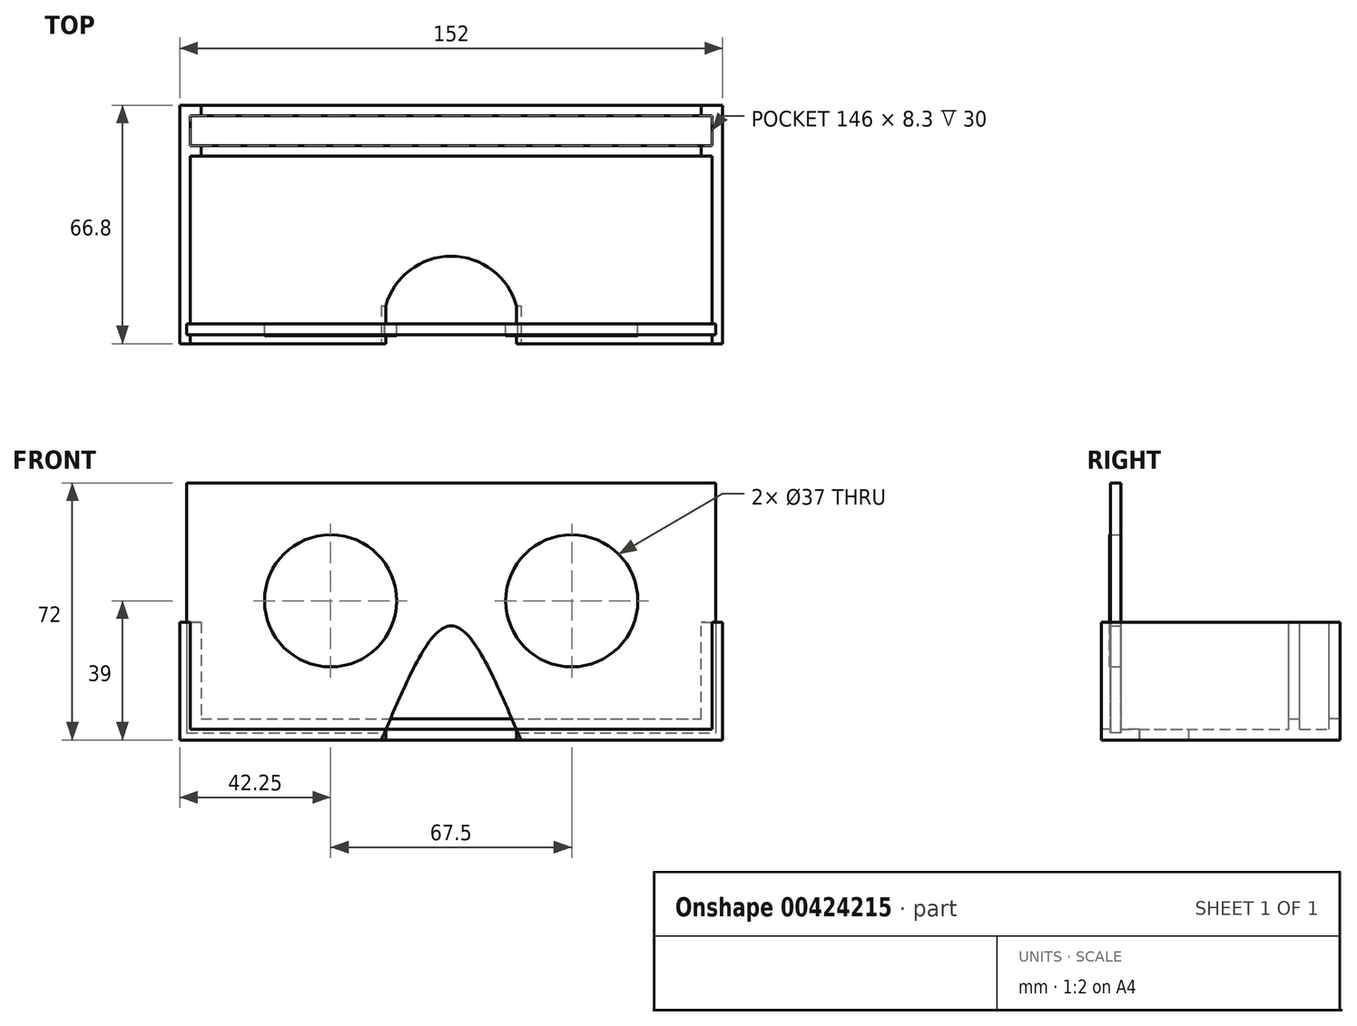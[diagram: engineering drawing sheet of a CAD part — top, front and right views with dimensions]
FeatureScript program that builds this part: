
annotation { "Feature Type Name" : "Feature", "Feature Type Description" : "" }
export const myFeature = defineFeature(function(context is Context, id is Id, definition is map)
    precondition{}
    {
        {
            var Q0;
            Q0=qCreatedBy(makeId("Front.planeOp"),FACE);
            var sketch = newSketch(context, id + "F0", { "sketchPlane" : qUnion([Q0])});
            skCircle(sketch, "E0", {"center": v(-33.75, 0) * mm, "radius": 18.5 * mm});
            skCircle(sketch, "E1", {"center": v(33.75, 0) * mm, "radius": 18.5 * mm});
            skLineSegment(sketch, "E2", {"start": v(0, 0) * mm, "end": v(15.25, 0) * mm});
            skLineSegment(sketch, "E3", {"start": v(0, 0) * mm, "end": v(-15.25, 0) * mm});
            skSolve(sketch);
        }
        {
            var Q0;
            Q0=makeQuery(id+"F0.imprint","IMPRINT",FACE,{"disambiguationData":[TD([[makeQuery(id+"F0.imprint","IMPRINT",EDGE,{"derivedFrom":sQuery(id+"F0.wireOp",EDGE,"E1")}),1.0]])]});
            var Q1;
            Q1=makeQuery(id+"F0.imprint","IMPRINT",FACE,{"disambiguationData":[TD([[makeQuery(id+"F0.imprint","IMPRINT",EDGE,{"derivedFrom":sQuery(id+"F0.wireOp",EDGE,"E0")}),1.0]])]});
            extrude(context, id + "F1", {"entities" : qUnion([Q0, Q1]), "depth" : 3.2 * mm});
        }
        {
            var Q0;
            Q0=qCreatedBy(makeId("Front.planeOp"),FACE);
            cPlane(context, id + "F2", {"entities" : qUnion([Q0]), "cplaneType" : CPlaneType.OFFSET, "offset" : 50 * mm, "oppositeDirection" : true, "width" : 150 * mm, "height" : 150 * mm});
        }
        {
            var Q0;
            Q0=qCreatedBy(id+"F2.planeOp",FACE);
            var sketch = newSketch(context, id + "F3", { "sketchPlane" : qUnion([Q0])});
            skLineSegment(sketch, "E4.bottom", {"start": v(-71.2, 34.8) * mm, "end": v(71.2, 34.8) * mm});
            skLineSegment(sketch, "E4.top", {"start": v(-71.2, -34.8) * mm, "end": v(71.2, -34.8) * mm});
            skLineSegment(sketch, "E4.left", {"start": v(-71.2, 34.8) * mm, "end": v(-71.2, -34.8) * mm});
            skLineSegment(sketch, "E4.right", {"start": v(71.2, 34.8) * mm, "end": v(71.2, -34.8) * mm});
            skLineSegment(sketch, "E5", {"start": v(0, 0) * mm, "end": v(0, 34.8) * mm, "construction": true});
            skLineSegment(sketch, "E6", {"start": v(0, 0) * mm, "end": v(-71.2, 0) * mm, "construction": true});
            skSolve(sketch);
        }
        {
            var Q0;
            Q0=qCreatedBy(id+"F2.planeOp",FACE);
            var sketch = newSketch(context, id + "F4", { "sketchPlane" : qUnion([Q0])});
            skLineSegment(sketch, "E7", {"start": v(-73, -6) * mm, "end": v(-76, -6) * mm});
            skLineSegment(sketch, "E8", {"start": v(-76, -6) * mm, "end": v(-76, -39) * mm});
            skLineSegment(sketch, "E9", {"start": v(-76, -39) * mm, "end": v(76, -39) * mm});
            skLineSegment(sketch, "E10", {"start": v(76, -39) * mm, "end": v(76, -6) * mm});
            skLineSegment(sketch, "E11", {"start": v(76, -6) * mm, "end": v(73, -6) * mm});
            skLineSegment(sketch, "E12", {"start": v(73, -6) * mm, "end": v(73, -36) * mm});
            skLineSegment(sketch, "E13", {"start": v(73, -36) * mm, "end": v(-73, -36) * mm});
            skLineSegment(sketch, "E14", {"start": v(-73, -36) * mm, "end": v(-73, -6) * mm});
            skLineSegment(sketch, "E15", {"start": v(-73, -6) * mm, "end": v(73, -6) * mm});
            skLineSegment(sketch, "E16", {"start": v(0, -36) * mm, "end": v(0, 0) * mm});
            skSolve(sketch);
        }
        {
            var Q0;
            Q0=makeQuery(id+"F4.imprint","IMPRINT",FACE,{"disambiguationData":[TD([[makeQuery(id+"F4.imprint","IMPRINT",EDGE,{"derivedFrom":sQuery(id+"F4.wireOp",EDGE,"E7")}),1.0]])]});
            extrude(context, id + "F5", {"entities" : qUnion([Q0]), "depth" : 55.5 * mm, "hasSecondDirection" : true, "secondDirectionOppositeDirection" : true, "secondDirectionDepth" : 11.3 * mm});
        }
        {
            var Q0;
            Q0=qCreatedBy(makeId("Front.planeOp"),FACE);
            var sketch = newSketch(context, id + "F6", { "sketchPlane" : qUnion([Q0])});
            skCircle(sketch, "E17", {"center": v(-33.75, 0) * mm, "radius": 18.5 * mm});
            skCircle(sketch, "E18", {"center": v(33.75, 0) * mm, "radius": 18.5 * mm});
            skLineSegment(sketch, "E19", {"start": v(-15.25, 0) * mm, "end": v(0, 0) * mm});
            skLineSegment(sketch, "E20", {"start": v(15.25, 0) * mm, "end": v(0, 0) * mm});
            skLineSegment(sketch, "E21.bottom", {"start": v(-74, 33) * mm, "end": v(74, 33) * mm});
            skLineSegment(sketch, "E21.top", {"start": v(-74, -37) * mm, "end": v(74, -37) * mm});
            skLineSegment(sketch, "E21.left", {"start": v(-74, 33) * mm, "end": v(-74, -37) * mm});
            skLineSegment(sketch, "E21.right", {"start": v(74, 33) * mm, "end": v(74, -37) * mm});
            skLineSegment(sketch, "E22", {"start": v(0, 0) * mm, "end": v(0, 33) * mm});
            skLineSegment(sketch, "E23.top", {"start": v(-74, 43) * mm, "end": v(74, 43) * mm});
            skLineSegment(sketch, "E23.left", {"start": v(-74, 33) * mm, "end": v(-74, 43) * mm});
            skLineSegment(sketch, "E23.right", {"start": v(74, 33) * mm, "end": v(74, 43) * mm});
            skSolve(sketch);
        }
        {
            var Q0;
            Q0=makeQuery(id+"F6.imprint","IMPRINT",FACE,{"disambiguationData":[TD([[makeQuery(id+"F6.imprint","IMPRINT",EDGE,{"derivedFrom":sQuery(id+"F6.wireOp",EDGE,"E17")}),-1.0]])]});
            var Q1;
            Q1=makeQuery(id+"F6.imprint","IMPRINT",FACE,{"disambiguationData":[TD([[makeQuery(id+"F6.imprint","IMPRINT",EDGE,{"derivedFrom":sQuery(id+"F6.wireOp",EDGE,"E23.top")}),-1.0]])]});
            extrude(context, id + "F7", {"entities" : qUnion([Q0, Q1]), "operationType" : NewBodyOperationType.REMOVE, "depth" : 3 * mm});
        }
        {
            var Q0;
            Q0=makeQuery(id+"F6.imprint","IMPRINT",FACE,{"disambiguationData":[TD([[makeQuery(id+"F6.imprint","IMPRINT",EDGE,{"derivedFrom":sQuery(id+"F6.wireOp",EDGE,"E17")}),-1.0]])]});
            extrude(context, id + "F8", {"entities" : qUnion([Q0]), "depth" : 3 * mm});
        }
        {
            var Q0;
            Q0=qCreatedBy(makeId("Front.planeOp"),FACE);
            var sketch = newSketch(context, id + "F9", { "sketchPlane" : qUnion([Q0])});
            skFitSpline(sketch, "E24", {"points": [v(-20, -40) * mm, v(0, -7) * mm, v(20, -40) * mm], "startDerivative": vector(42.04, 95.95) * mm, "endDerivative": vector(42.04, -95.95) * mm});
            skLineSegment(sketch, "E25", {"start": v(-20, -40) * mm, "end": v(20, -40) * mm});
            skLineSegment(sketch, "E26", {"start": v(-20, -40) * mm, "end": v(-13, -24) * mm});
            skLineSegment(sketch, "E27", {"start": v(13, -24) * mm, "end": v(20, -40) * mm});
            skLineSegment(sketch, "E28", {"start": v(0, -40) * mm, "end": v(0, 0) * mm});
            skSolve(sketch);
        }
        {
            var Q0;
            Q0 = qSketchRegion(id + "F9", true);
            extrude(context, id + "F10", {"entities" : qUnion([Q0]), "operationType" : NewBodyOperationType.REMOVE, "depth" : 26.3 * mm, "hasSecondDirection" : true, "secondDirectionOppositeDirection" : true, "secondDirectionDepth" : 5.1 * mm});
        }
        {
            var Q0;
            Q0=qCreatedBy(makeId("Top.planeOp"),FACE);
            var sketch = newSketch(context, id + "F11", { "sketchPlane" : qUnion([Q0])});
            skCircle(sketch, "E29", {"center": v(0, 0) * mm, "radius": 19 * mm});
            skLineSegment(sketch, "E30", {"start": v(-18.33, 5) * mm, "end": v(18.33, 5) * mm});
            skSolve(sketch);
        }
        {
            var Q0;
            {var subQ0=sQuery(id+"F11.wireOp",EDGE,"E30");Q0=makeQuery(id+"F11.imprint","IMPRINT",FACE,{"disambiguationData":[TD([[makeQuery(id+"F11.imprint","IMPRINT",EDGE,{"derivedFrom":subQ0}),1.0]])]});}
            extrude(context, id + "F12", {"entities" : qUnion([Q0]), "operationType" : NewBodyOperationType.REMOVE, "oppositeDirection" : true, "depth" : 63.1 * mm});
        }
        {
            var Q0;
            Q0=qCreatedBy(id+"F2.planeOp",FACE);
            var sketch = newSketch(context, id + "F13", { "sketchPlane" : qUnion([Q0])});
            skLineSegment(sketch, "E31", {"start": v(73, -6) * mm, "end": v(73, -36) * mm});
            skLineSegment(sketch, "E32", {"start": v(73, -36) * mm, "end": v(-73, -36) * mm});
            skLineSegment(sketch, "E33", {"start": v(-73, -36) * mm, "end": v(-73, -6) * mm});
            skLineSegment(sketch, "E34", {"start": v(-73, -6) * mm, "end": v(-70, -6) * mm});
            skLineSegment(sketch, "E35", {"start": v(-70, -6) * mm, "end": v(-70, -33) * mm});
            skLineSegment(sketch, "E36", {"start": v(-70, -33) * mm, "end": v(70, -33) * mm});
            skLineSegment(sketch, "E37", {"start": v(70, -33) * mm, "end": v(70, -6) * mm});
            skLineSegment(sketch, "E38", {"start": v(70, -6) * mm, "end": v(73, -6) * mm});
            skLineSegment(sketch, "E39", {"start": v(0, -36) * mm, "end": v(0, 0) * mm, "construction": true});
            skPoint(sketch, "E39.startSnap0", {"position": v(0, -33) * mm});
            skSolve(sketch);
        }
        {
            var Q0;
            Q0=makeQuery(id+"F13.imprint","IMPRINT",FACE,{"disambiguationData":[TD([[makeQuery(id+"F13.imprint","IMPRINT",EDGE,{"derivedFrom":sQuery(id+"F13.wireOp",EDGE,"E31")}),-1.0]])]});
            extrude(context, id + "F14", {"entities" : qUnion([Q0]), "operationType" : NewBodyOperationType.ADD, "depth" : 3 * mm});
        }
        {
            var Q0;
            Q0=qCreatedBy(id+"F2.planeOp",FACE);
            cPlane(context, id + "F15", {"entities" : qUnion([Q0]), "cplaneType" : CPlaneType.OFFSET, "offset" : 8.3 * mm, "oppositeDirection" : true, "width" : 150 * mm, "height" : 150 * mm});
        }
        {
            var Q0;
            Q0=qCreatedBy(id+"F15.planeOp",FACE);
            var sketch = newSketch(context, id + "F16", { "sketchPlane" : qUnion([Q0])});
            skLineSegment(sketch, "E40", {"start": v(73, -6) * mm, "end": v(73, -36) * mm});
            skLineSegment(sketch, "E41", {"start": v(73, -36) * mm, "end": v(-73, -36) * mm});
            skLineSegment(sketch, "E42", {"start": v(-73, -36) * mm, "end": v(-73, -6) * mm});
            skLineSegment(sketch, "E43", {"start": v(-73, -6) * mm, "end": v(-70, -6) * mm});
            skLineSegment(sketch, "E44", {"start": v(-70, -6) * mm, "end": v(-70, -33) * mm});
            skLineSegment(sketch, "E45", {"start": v(-70, -33) * mm, "end": v(70, -33) * mm});
            skLineSegment(sketch, "E46", {"start": v(70, -33) * mm, "end": v(70, -6) * mm});
            skLineSegment(sketch, "E47", {"start": v(70, -6) * mm, "end": v(73, -6) * mm});
            skLineSegment(sketch, "E48", {"start": v(0, -36) * mm, "end": v(0, 0) * mm, "construction": true});
            skPoint(sketch, "E48.startSnap0", {"position": v(0, -33) * mm});
            skSolve(sketch);
        }
        {
            var Q0;
            Q0 = qSketchRegion(id + "F16", true);
            extrude(context, id + "F17", {"entities" : qUnion([Q0]), "operationType" : NewBodyOperationType.ADD, "oppositeDirection" : true, "depth" : 3 * mm});
        }
    });
